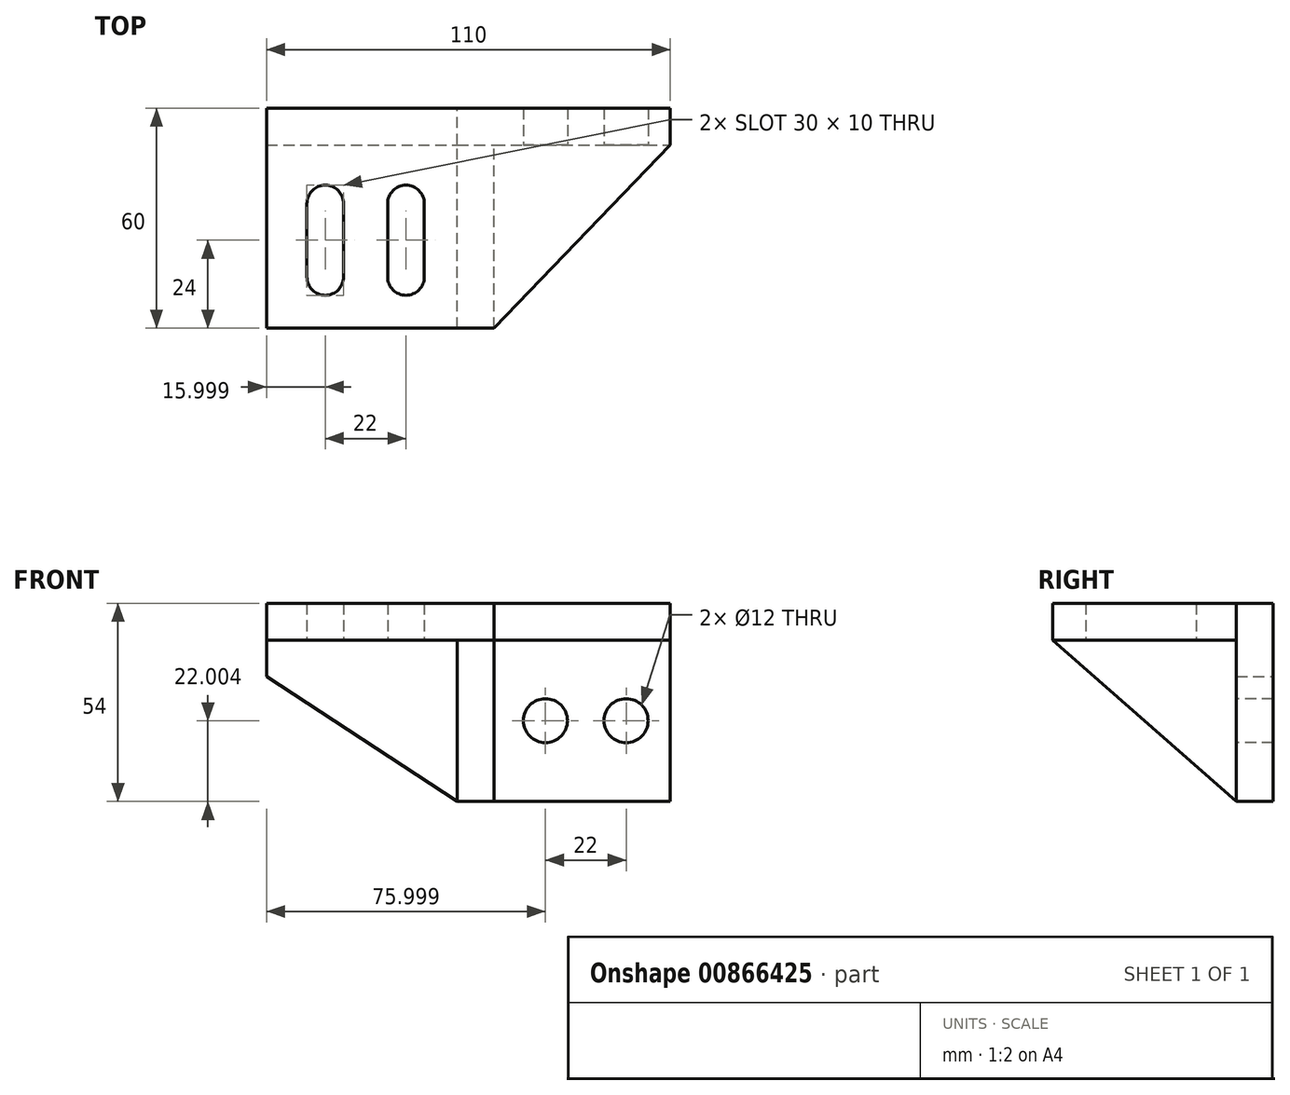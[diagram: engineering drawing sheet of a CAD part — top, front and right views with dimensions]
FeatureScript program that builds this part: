
annotation { "Feature Type Name" : "Feature", "Feature Type Description" : "" }
export const myFeature = defineFeature(function(context is Context, id is Id, definition is map)
    precondition{}
    {
        {
            var Q0;
            Q0=qCreatedBy(makeId("Front.planeOp"),FACE);
            var sketch = newSketch(context, id + "F0", { "sketchPlane" : qUnion([Q0])});
            skLineSegment(sketch, "E0", {"start": v(-74.76, 27.32) * mm, "end": v(35.24, 27.32) * mm});
            skLineSegment(sketch, "E1", {"start": v(35.24, 27.32) * mm, "end": v(35.24, -26.68) * mm});
            skLineSegment(sketch, "E2", {"start": v(35.24, -26.68) * mm, "end": v(-22.76, -26.68) * mm});
            skLineSegment(sketch, "E3", {"start": v(-22.76, -26.68) * mm, "end": v(-74.76, 7.32) * mm});
            skLineSegment(sketch, "E4", {"start": v(-74.76, 7.32) * mm, "end": v(-74.76, 27.32) * mm});
            skSolve(sketch);
        }
        {
            var Q0;
            Q0=makeQuery(id+"F0.imprint","IMPRINT",FACE,{"disambiguationData":[TD([[makeQuery(id+"F0.imprint","IMPRINT",EDGE,{"derivedFrom":sQuery(id+"F0.wireOp",EDGE,"E0")}),-1.0]])]});
            extrude(context, id + "F1", {"entities" : qUnion([Q0]), "depth" : 10 * mm, "offsetDistance" : 25 * mm});
        }
        {
            var Q0;
            Q0=makeQuery(id+"F1.opExtrude","CAP_FACE",FACE,{"disambiguationData":[OSD([sQuery(id+"F0.wireOp",EDGE,"E0"),sQuery(id+"F0.wireOp",EDGE,"E1"),sQuery(id+"F0.wireOp",EDGE,"E2"),sQuery(id+"F0.wireOp",EDGE,"E3"),sQuery(id+"F0.wireOp",EDGE,"E4")])],"isStart":false});
            var sketch = newSketch(context, id + "F2", { "sketchPlane" : qUnion([Q0])});
            skLineSegment(sketch, "E5", {"start": v(-74.76, 27.32) * mm, "end": v(-74.76, 17.32) * mm});
            skLineSegment(sketch, "E6", {"start": v(-74.76, 17.32) * mm, "end": v(35.24, 17.32) * mm});
            skSolve(sketch);
        }
        {
            var Q0;
            Q0=makeQuery(id+"F2.imprint","IMPRINT",FACE,{"disambiguationData":[TD([[makeQuery(id+"F2.imprint","IMPRINT",EDGE,{"derivedFrom":sQuery(id+"F2.wireOp",EDGE,"E5")}),-1.0]])]});
            extrude(context, id + "F3", {"entities" : qUnion([Q0]), "operationType" : NewBodyOperationType.ADD, "depth" : 50 * mm, "offsetDistance" : 25 * mm});
        }
        {
            var Q0;
            Q0=makeQuery(id+"F1.opExtrude","CAP_FACE",FACE,{"disambiguationData":[OSD([sQuery(id+"F0.wireOp",EDGE,"E0"),sQuery(id+"F0.wireOp",EDGE,"E1"),sQuery(id+"F0.wireOp",EDGE,"E2"),sQuery(id+"F0.wireOp",EDGE,"E3"),sQuery(id+"F0.wireOp",EDGE,"E4")])],"isStart":false});
            var sketch = newSketch(context, id + "F4", { "sketchPlane" : qUnion([Q0])});
            skLineSegment(sketch, "E7", {"start": v(-22.76, -26.68) * mm, "end": v(-22.76, 17.32) * mm});
            skLineSegment(sketch, "E8", {"start": v(-22.76, 17.32) * mm, "end": v(-12.76, 17.32) * mm});
            skLineSegment(sketch, "E9", {"start": v(-12.76, 17.32) * mm, "end": v(-12.76, -26.68) * mm});
            skLineSegment(sketch, "E10", {"start": v(-12.76, -26.68) * mm, "end": v(-22.76, -26.68) * mm});
            skSolve(sketch);
        }
        {
            var Q0;
            Q0 = qSketchRegion(id + "F4", true);
            extrude(context, id + "F5", {"entities" : qUnion([Q0]), "operationType" : NewBodyOperationType.ADD, "depth" : 50 * mm, "offsetDistance" : 25 * mm});
        }
        {
            var Q0;
            Q0=makeQuery(id+"F5.opExtrude","SWEPT_FACE",FACE,{"disambiguationData":[OSD([sQuery(id+"F4.wireOp",EDGE,"E9")])]});
            var sketch = newSketch(context, id + "F6", { "sketchPlane" : qUnion([Q0])});
            skLineSegment(sketch, "E11", {"start": v(-60, 17.32) * mm, "end": v(-10, -26.68) * mm});
            skSolve(sketch);
        }
        {
            var Q0;
            Q0 = qSketchRegion(id + "F6", true);
            var Q1;
            Q1=makeQuery(id+"F6.imprint","IMPRINT",FACE,{"disambiguationData":[TD([[makeQuery(id+"F6.imprint","IMPRINT",EDGE,{"derivedFrom":sQuery(id+"F6.wireOp",EDGE,"E11")}),-1.0]])]});
            extrude(context, id + "F7", {"entities" : qUnion([Q0, Q1]), "operationType" : NewBodyOperationType.REMOVE, "oppositeDirection" : true, "depth" : 11 * mm, "offsetDistance" : 25 * mm});
        }
        {
            var Q0;
            {var subQ0=sQuery(id+"F2.wireOp",EDGE,"E6");var subQ1=sQuery(id+"F0.wireOp",EDGE,"E1");Q0=makeQuery(id+"F5.boolean.opBoolean","SPLIT",FACE,{"disambiguationData":[TD([makeQuery(id+"F1.opExtrude","SWEPT_FACE",FACE,{"disambiguationData":[OSD([subQ1])]})])],"derivedFrom":makeQuery(id+"F3.opExtrude","SWEPT_FACE",FACE,{"disambiguationData":[OSD([subQ0])]})});}
            var sketch = newSketch(context, id + "F8", { "sketchPlane" : qUnion([Q0])});
            skLineSegment(sketch, "E12", {"start": v(-12.76, 60) * mm, "end": v(35.24, 10) * mm});
            skSolve(sketch);
        }
        {
            var Q0;
            Q0 = qSketchRegion(id + "F8", true);
            var Q1;
            Q1=makeQuery(id+"F8.imprint","IMPRINT",FACE,{"disambiguationData":[TD([[makeQuery(id+"F8.imprint","IMPRINT",EDGE,{"derivedFrom":sQuery(id+"F8.wireOp",EDGE,"E12")}),1.0]])]});
            extrude(context, id + "F9", {"entities" : qUnion([Q0, Q1]), "operationType" : NewBodyOperationType.REMOVE, "oppositeDirection" : true, "depth" : 25 * mm, "offsetDistance" : 25 * mm});
        }
        {
            var Q0;
            {var subQ0=sQuery(id+"F0.wireOp",EDGE,"E2");var subQ1=sQuery(id+"F0.wireOp",EDGE,"E1");Q0=makeQuery(id+"F5.boolean.opBoolean","SPLIT",FACE,{"disambiguationData":[TD([makeQuery(id+"F1.opExtrude","SWEPT_FACE",FACE,{"disambiguationData":[OSD([subQ1])]})])],"derivedFrom":makeQuery(id+"F1.opExtrude","CAP_FACE",FACE,{"disambiguationData":[OSD([sQuery(id+"F0.wireOp",EDGE,"E0"),subQ1,subQ0,sQuery(id+"F0.wireOp",EDGE,"E3"),sQuery(id+"F0.wireOp",EDGE,"E4")])],"isStart":false})});}
            var sketch = newSketch(context, id + "F10", { "sketchPlane" : qUnion([Q0])});
            skCircle(sketch, "E13", {"center": v(23.24, -4.68) * mm, "radius": 6 * mm});
            skCircle(sketch, "E14", {"center": v(1.24, -4.68) * mm, "radius": 6 * mm});
            skSolve(sketch);
        }
        {
            var Q0;
            Q0 = qSketchRegion(id + "F10", true);
            extrude(context, id + "F11", {"entities" : qUnion([Q0]), "operationType" : NewBodyOperationType.REMOVE, "oppositeDirection" : true, "depth" : 11 * mm, "offsetDistance" : 25 * mm});
        }
        {
            var Q0;
            {var subQ0=sQuery(id+"F2.wireOp",EDGE,"E6");var subQ4=sQuery(id+"F0.wireOp",EDGE,"E4");Q0=makeQuery(id+"F5.boolean.opBoolean","SPLIT",FACE,{"disambiguationData":[TD([makeQuery(id+"F1.opExtrude","SWEPT_FACE",FACE,{"disambiguationData":[OSD([subQ4])]})])],"derivedFrom":makeQuery(id+"F3.opExtrude","SWEPT_FACE",FACE,{"disambiguationData":[OSD([subQ0])]})});}
            var sketch = newSketch(context, id + "F12", { "sketchPlane" : qUnion([Q0])});
            skLineSegment(sketch, "E15", {"start": v(-63.76, 46) * mm, "end": v(-63.76, 26) * mm});
            skArc(sketch, "E16", {"start": v(-63.76, 26) * mm, "mid": v(-58.76, 21) * mm, "end": v(-53.76, 26) * mm});
            skLineSegment(sketch, "E17", {"start": v(-53.76, 26) * mm, "end": v(-53.76, 46) * mm});
            skArc(sketch, "E18", {"start": v(-53.76, 46) * mm, "mid": v(-58.76, 51) * mm, "end": v(-63.76, 46) * mm});
            skLineSegment(sketch, "E19", {"start": v(-41.76, 26) * mm, "end": v(-41.76, 46) * mm});
            skArc(sketch, "E20", {"start": v(-31.76, 46) * mm, "mid": v(-36.76, 51) * mm, "end": v(-41.76, 46) * mm});
            skLineSegment(sketch, "E21", {"start": v(-31.76, 46) * mm, "end": v(-31.76, 26) * mm});
            skArc(sketch, "E22", {"start": v(-41.76, 26) * mm, "mid": v(-36.76, 21) * mm, "end": v(-31.76, 26) * mm});
            skSolve(sketch);
        }
        {
            var Q0;
            Q0=makeQuery(id+"F12.imprint","IMPRINT",FACE,{"disambiguationData":[TD([[makeQuery(id+"F12.imprint","IMPRINT",EDGE,{"derivedFrom":sQuery(id+"F12.wireOp",EDGE,"E15")}),1.0]])]});
            var Q1;
            Q1=makeQuery(id+"F12.imprint","IMPRINT",FACE,{"disambiguationData":[TD([[makeQuery(id+"F12.imprint","IMPRINT",EDGE,{"derivedFrom":sQuery(id+"F12.wireOp",EDGE,"E19")}),-1.0]])]});
            extrude(context, id + "F13", {"entities" : qUnion([Q0, Q1]), "operationType" : NewBodyOperationType.REMOVE, "oppositeDirection" : true, "depth" : 11 * mm, "offsetDistance" : 25 * mm});
        }
    });
